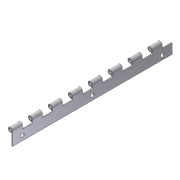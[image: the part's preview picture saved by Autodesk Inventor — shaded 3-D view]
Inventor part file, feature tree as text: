
AUTODESK INVENTOR PART (.ipt)
format: ipt  version: 2012 (Build 160160000, 160)  size: 161,792 bytes
history: native  units: in
note: dims shown in document units (in); Inventor stores cm internally (conversion verified against a paired STEP export)
features: extrude x3, sketch x3, fillet x1, pattern_linear x1, projected_geometry x1
ambient origin geometry x8: Origin, YZ Plane, XZ Plane, XY Plane, X Axis, Y Axis, Z Axis, Center Point
bodies: Solid1 (feature_tree)
feature tree (9):
  extrude  "Extrusion1"  Depth=0.09in
  extrude  "Extrusion2"  Depth=16.0in TaperAngle=0.0deg
  fillet  "Fillet1"  Radius=1.0in
  pattern_linear  "Rectangular Pattern1"  Spacing1=0.125in  [1 undecoded]
  extrude  "Extrusion3"  Depth=16.0in TaperAngle=0.0deg
  sketch  "Sketch1"  dims[d0=0.445in d1=0.09in]
  sketch  "Sketch2"  dims[d2=0.09in d3=16.0in d4=0.0in d5=1.0in]
  projected_geometry  "Projected Loop1"
  sketch  "Sketch3"  dims[d6=1.0in d7=0.125in d8=16.0in d9=0.0in d10=0.125in d11=3.1496in d13=2.0in d14=0.375in d15=1.0in d16=8.0in d17=1.0in d18=0.375in d19=0.375in d20=1.0in d21=0.0in]
note: 1 required parameter value undecoded (feature->parameter linkage not recoverable at this tier; creation-order binding heuristic only, values carry confidence <= 0.55)
